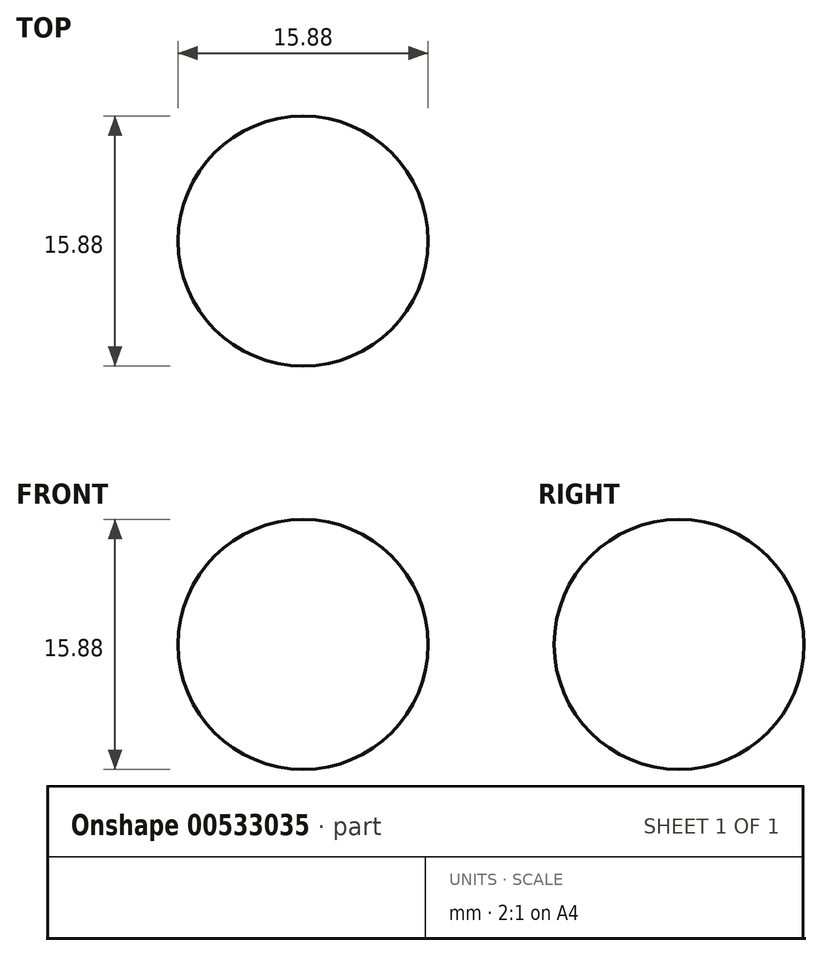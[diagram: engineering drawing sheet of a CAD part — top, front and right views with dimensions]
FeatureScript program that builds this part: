
annotation { "Feature Type Name" : "Feature", "Feature Type Description" : "" }
export const myFeature = defineFeature(function(context is Context, id is Id, definition is map)
    precondition{}
    {
        {
            var Q0;
            Q0=qCreatedBy(makeId("Front.planeOp"),FACE);
            var sketch = newSketch(context, id + "F0", { "sketchPlane" : qUnion([Q0])});
            skArc(sketch, "E0", {"start": v(0, 7.94) * mm, "mid": v(-7.94, 0) * mm, "end": v(0, -7.94) * mm});
            skLineSegment(sketch, "E1", {"start": v(0, 7.94) * mm, "end": v(0, -7.94) * mm});
            skSolve(sketch);
        }
        {
            var Q0;
            Q0=qCreatedBy(makeId("Front.planeOp"),FACE);
            var sketch = newSketch(context, id + "F1", { "sketchPlane" : qUnion([Q0])});
            skLineSegment(sketch, "E2", {"start": v(0, 27.62) * mm, "end": v(0, -26.59) * mm, "construction": true});
            skSolve(sketch);
        }
        {
            var Q0;
            Q0=makeQuery(id+"F0.imprint","IMPRINT",FACE,{"disambiguationData":[TD([[makeQuery(id+"F0.imprint","IMPRINT",EDGE,{"derivedFrom":sQuery(id+"F0.wireOp",EDGE,"E0")}),1.0]])]});
            var Q1;
            Q1=sQuery(id+"F1.wireOp",EDGE,"E2");
            revolve(context, id + "F2", {"surfaceOperationType" : NewSurfaceOperationType.NEW, "entities" : qUnion([Q0]), "axis" : qUnion([Q1]), "revolveType" : RevolveType.FULL});
        }
    });
